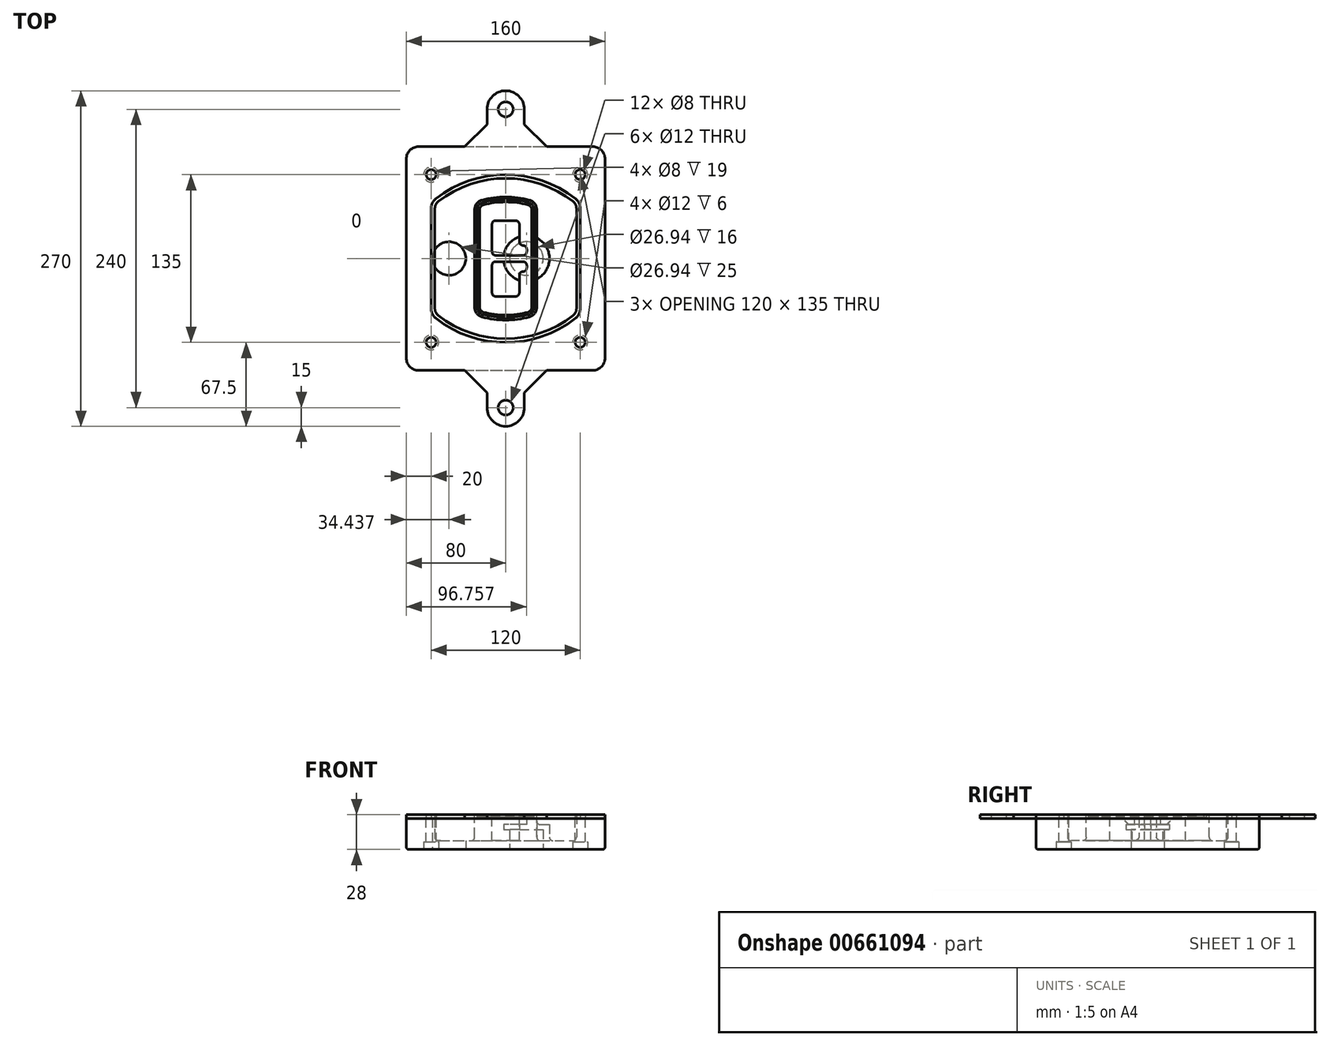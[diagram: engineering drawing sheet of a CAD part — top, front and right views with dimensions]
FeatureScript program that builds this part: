
annotation { "Feature Type Name" : "Feature", "Feature Type Description" : "" }
export const myFeature = defineFeature(function(context is Context, id is Id, definition is map)
    precondition{}
    {
        {
            var Q0;
            Q0=qCreatedBy(makeId("Top.planeOp"),FACE);
            var sketch = newSketch(context, id + "F0", { "sketchPlane" : qUnion([Q0])});
            skPoint(sketch, "E0.rect.middle", {"position": v(0, 0) * mm});
            skLineSegment(sketch, "E1.bottom", {"start": v(-70, -90) * mm, "end": v(70, -90) * mm});
            skLineSegment(sketch, "E1.top", {"start": v(-70, 90) * mm, "end": v(70, 90) * mm});
            skLineSegment(sketch, "E1.left", {"start": v(-80, -80) * mm, "end": v(-80, 80) * mm});
            skLineSegment(sketch, "E1.right", {"start": v(80, -80) * mm, "end": v(80, 80) * mm});
            skLineSegment(sketch, "E2", {"start": v(-80, 90) * mm, "end": v(80, -90) * mm, "construction": true});
            skLineSegment(sketch, "E3", {"start": v(80, 90) * mm, "end": v(-80, -90) * mm, "construction": true});
            skCircle(sketch, "E4", {"center": v(-60, 67.5) * mm, "radius": 4 * mm});
            skCircle(sketch, "E5", {"center": v(60, 67.5) * mm, "radius": 4 * mm});
            skCircle(sketch, "E6", {"center": v(60, -67.5) * mm, "radius": 4 * mm});
            skCircle(sketch, "E7", {"center": v(-60, -67.5) * mm, "radius": 4 * mm});
            skLineSegment(sketch, "E8", {"start": v(-60, 67.5) * mm, "end": v(60, 67.5) * mm, "construction": true});
            skLineSegment(sketch, "E9", {"start": v(60, 67.5) * mm, "end": v(60, -67.5) * mm, "construction": true});
            skLineSegment(sketch, "E10", {"start": v(60, -67.5) * mm, "end": v(-60, -67.5) * mm, "construction": true});
            skLineSegment(sketch, "E11", {"start": v(-60, -67.5) * mm, "end": v(-60, 67.5) * mm, "construction": true});
            skLineSegment(sketch, "E12", {"start": v(-60, 40.3) * mm, "end": v(-60, -40.3) * mm});
            skLineSegment(sketch, "E13", {"start": v(60, 40.3) * mm, "end": v(60, -40.3) * mm});
            skArc(sketch, "E14", {"start": v(56.15, 48.18) * mm, "mid": v(0, 67.5) * mm, "end": v(-56.15, 48.18) * mm});
            skArc(sketch, "E15", {"start": v(-56.15, -48.18) * mm, "mid": v(0, -67.5) * mm, "end": v(56.15, -48.18) * mm});
            skLineSegment(sketch, "E16", {"start": v(-60, 0) * mm, "end": v(60, 0) * mm, "construction": true});
            skPoint(sketch, "E17.visualSharp", {"position": v(-60, -45) * mm});
            skArc(sketch, "E17.filletArc", {"start": v(-60, -40.3) * mm, "mid": v(-58.99, -44.68) * mm, "end": v(-56.15, -48.18) * mm});
            skPoint(sketch, "E18.visualSharp", {"position": v(-60, 45) * mm});
            skArc(sketch, "E18.filletArc", {"start": v(-56.15, 48.18) * mm, "mid": v(-58.99, 44.68) * mm, "end": v(-60, 40.3) * mm});
            skPoint(sketch, "E19.visualSharp", {"position": v(60, 45) * mm});
            skArc(sketch, "E19.filletArc", {"start": v(60, 40.3) * mm, "mid": v(58.99, 44.68) * mm, "end": v(56.15, 48.18) * mm});
            skPoint(sketch, "E20.visualSharp", {"position": v(60, -45) * mm});
            skArc(sketch, "E20.filletArc", {"start": v(56.15, -48.18) * mm, "mid": v(58.99, -44.68) * mm, "end": v(60, -40.3) * mm});
            skPoint(sketch, "E21.visualSharp", {"position": v(-80, 90) * mm});
            skArc(sketch, "E21.filletArc", {"start": v(-70, 90) * mm, "mid": v(-77.07, 87.07) * mm, "end": v(-80, 80) * mm});
            skPoint(sketch, "E22.visualSharp", {"position": v(80, 90) * mm});
            skArc(sketch, "E22.filletArc", {"start": v(80, 80) * mm, "mid": v(77.07, 87.07) * mm, "end": v(70, 90) * mm});
            skPoint(sketch, "E23.visualSharp", {"position": v(80, -90) * mm});
            skArc(sketch, "E23.filletArc", {"start": v(70, -90) * mm, "mid": v(77.07, -87.07) * mm, "end": v(80, -80) * mm});
            skPoint(sketch, "E24.visualSharp", {"position": v(-80, -90) * mm});
            skArc(sketch, "E24.filletArc", {"start": v(-80, -80) * mm, "mid": v(-77.07, -87.07) * mm, "end": v(-70, -90) * mm});
            skArc(sketch, "E25.0", {"start": v(57, 40.3) * mm, "mid": v(56.3, 43.36) * mm, "end": v(54.3, 45.81) * mm});
            skLineSegment(sketch, "E25.1", {"start": v(57, 40.3) * mm, "end": v(57, -40.3) * mm});
            skArc(sketch, "E25.2", {"start": v(54.3, -45.81) * mm, "mid": v(56.3, -43.36) * mm, "end": v(57, -40.3) * mm});
            skArc(sketch, "E25.3", {"start": v(-54.3, -45.81) * mm, "mid": v(0, -64.5) * mm, "end": v(54.3, -45.81) * mm});
            skArc(sketch, "E25.4", {"start": v(-57, -40.3) * mm, "mid": v(-56.3, -43.36) * mm, "end": v(-54.3, -45.81) * mm});
            skArc(sketch, "E25.5", {"start": v(54.3, 45.81) * mm, "mid": v(0, 64.5) * mm, "end": v(-54.3, 45.81) * mm});
            skLineSegment(sketch, "E25.6", {"start": v(-57, 40.3) * mm, "end": v(-57, -40.3) * mm});
            skArc(sketch, "E25.7", {"start": v(-54.3, 45.81) * mm, "mid": v(-56.3, 43.36) * mm, "end": v(-57, 40.3) * mm});
            skArc(sketch, "E26.0", {"start": v(-58.62, 51.33) * mm, "mid": v(-62.58, 46.43) * mm, "end": v(-64, 40.3) * mm});
            skArc(sketch, "E26.1", {"start": v(58.62, 51.33) * mm, "mid": v(0, 71.5) * mm, "end": v(-58.62, 51.33) * mm});
            skArc(sketch, "E26.2", {"start": v(64, 40.3) * mm, "mid": v(62.58, 46.43) * mm, "end": v(58.62, 51.33) * mm});
            skLineSegment(sketch, "E26.3", {"start": v(64, 40.3) * mm, "end": v(64, -40.3) * mm});
            skArc(sketch, "E26.4", {"start": v(58.62, -51.33) * mm, "mid": v(62.58, -46.43) * mm, "end": v(64, -40.3) * mm});
            skLineSegment(sketch, "E26.5", {"start": v(-64, 40.3) * mm, "end": v(-64, -40.3) * mm});
            skArc(sketch, "E26.6", {"start": v(-58.62, -51.33) * mm, "mid": v(0, -71.5) * mm, "end": v(58.62, -51.33) * mm});
            skArc(sketch, "E26.7", {"start": v(-64, -40.3) * mm, "mid": v(-62.58, -46.43) * mm, "end": v(-58.62, -51.33) * mm});
            skSolve(sketch);
        }
        {
            var Q0;
            Q0=makeQuery(id+"F0.imprint","IMPRINT",FACE,{"disambiguationData":[TD([[makeQuery(id+"F0.imprint","IMPRINT",EDGE,{"derivedFrom":sQuery(id+"F0.wireOp",EDGE,"E1.bottom")}),1.0]])]});
            var Q1;
            Q1=makeQuery(id+"F0.imprint","IMPRINT",FACE,{"disambiguationData":[TD([[makeQuery(id+"F0.imprint","IMPRINT",EDGE,{"derivedFrom":sQuery(id+"F0.wireOp",EDGE,"E12")}),1.0]])]});
            var Q2;
            Q2=makeQuery(id+"F0.imprint","IMPRINT",FACE,{"disambiguationData":[TD([[makeQuery(id+"F0.imprint","IMPRINT",EDGE,{"derivedFrom":sQuery(id+"F0.wireOp",EDGE,"E25.0")}),1.0]])]});
            var Q3;
            Q3=makeQuery(id+"F0.imprint","IMPRINT",FACE,{"disambiguationData":[TD([[makeQuery(id+"F0.imprint","IMPRINT",EDGE,{"derivedFrom":sQuery(id+"F0.wireOp",EDGE,"E12")}),-1.0]])]});
            extrude(context, id + "F1", {"entities" : qUnion([Q0, Q1, Q2, Q3]), "oppositeDirection" : true, "depth" : 25 * mm});
        }
        {
            var Q0;
            Q0=makeQuery(id+"F0.imprint","IMPRINT",FACE,{"disambiguationData":[TD([[makeQuery(id+"F0.imprint","IMPRINT",EDGE,{"derivedFrom":sQuery(id+"F0.wireOp",EDGE,"E12")}),1.0]])]});
            extrude(context, id + "F2", {"entities" : qUnion([Q0]), "operationType" : NewBodyOperationType.ADD, "depth" : 3 * mm});
        }
        {
            var Q0;
            Q0=makeQuery(id+"F0.imprint","IMPRINT",FACE,{"disambiguationData":[TD([[makeQuery(id+"F0.imprint","IMPRINT",EDGE,{"derivedFrom":sQuery(id+"F0.wireOp",EDGE,"E25.0")}),1.0]])]});
            extrude(context, id + "F3", {"entities" : qUnion([Q0]), "operationType" : NewBodyOperationType.REMOVE, "oppositeDirection" : true, "depth" : 18 * mm});
        }
        {
            var Q0;
            Q0=makeQuery(id+"F2.opExtrude","CAP_FACE",FACE,{"disambiguationData":[OSD([sQuery(id+"F0.wireOp",EDGE,"E12"),sQuery(id+"F0.wireOp",EDGE,"E13"),sQuery(id+"F0.wireOp",EDGE,"E14"),sQuery(id+"F0.wireOp",EDGE,"E15"),sQuery(id+"F0.wireOp",EDGE,"E17.filletArc"),sQuery(id+"F0.wireOp",EDGE,"E18.filletArc"),sQuery(id+"F0.wireOp",EDGE,"E19.filletArc"),sQuery(id+"F0.wireOp",EDGE,"E20.filletArc"),sQuery(id+"F0.wireOp",EDGE,"E25.0"),sQuery(id+"F0.wireOp",EDGE,"E25.1"),sQuery(id+"F0.wireOp",EDGE,"E25.2"),sQuery(id+"F0.wireOp",EDGE,"E25.3"),sQuery(id+"F0.wireOp",EDGE,"E25.4"),sQuery(id+"F0.wireOp",EDGE,"E25.5"),sQuery(id+"F0.wireOp",EDGE,"E25.6"),sQuery(id+"F0.wireOp",EDGE,"E25.7")])],"isStart":false});
            var sketch = newSketch(context, id + "F4", { "sketchPlane" : qUnion([Q0])});
            skArc(sketch, "E27.0", {"start": v(-19.08, -46.97) * mm, "mid": v(0, -49.5) * mm, "end": v(19.08, -46.97) * mm});
            skArc(sketch, "E28.0", {"start": v(19.08, 46.97) * mm, "mid": v(0, 49.5) * mm, "end": v(-19.08, 46.97) * mm});
            skLineSegment(sketch, "E29", {"start": v(-25, 39.25) * mm, "end": v(-25, -39.25) * mm});
            skLineSegment(sketch, "E30", {"start": v(25, 39.25) * mm, "end": v(25, -39.25) * mm});
            skLineSegment(sketch, "E31", {"start": v(-25, 45.1) * mm, "end": v(25, 45.1) * mm, "construction": true});
            skLineSegment(sketch, "E32", {"start": v(-25, -45.1) * mm, "end": v(25, -45.1) * mm, "construction": true});
            skPoint(sketch, "E33.visualSharp", {"position": v(-25, 45.1) * mm});
            skArc(sketch, "E33.filletArc", {"start": v(-19.08, 46.97) * mm, "mid": v(-23.35, 44.11) * mm, "end": v(-25, 39.25) * mm});
            skPoint(sketch, "E34.visualSharp", {"position": v(25, 45.1) * mm});
            skArc(sketch, "E34.filletArc", {"start": v(25, 39.25) * mm, "mid": v(23.35, 44.11) * mm, "end": v(19.08, 46.97) * mm});
            skPoint(sketch, "E35.visualSharp", {"position": v(25, -45.1) * mm});
            skArc(sketch, "E35.filletArc", {"start": v(19.08, -46.97) * mm, "mid": v(23.35, -44.11) * mm, "end": v(25, -39.25) * mm});
            skPoint(sketch, "E36.visualSharp", {"position": v(-25, -45.1) * mm});
            skArc(sketch, "E36.filletArc", {"start": v(-25, -39.25) * mm, "mid": v(-23.35, -44.11) * mm, "end": v(-19.08, -46.97) * mm});
            skArc(sketch, "E37.0", {"start": v(54.3, 45.81) * mm, "mid": v(0, 64.5) * mm, "end": v(-54.3, 45.81) * mm});
            skArc(sketch, "E37.1", {"start": v(-54.3, 45.81) * mm, "mid": v(-56.3, 43.36) * mm, "end": v(-57, 40.3) * mm});
            skLineSegment(sketch, "E37.2", {"start": v(-57, 40.3) * mm, "end": v(-57, -40.3) * mm});
            skArc(sketch, "E37.3", {"start": v(-57, -40.3) * mm, "mid": v(-56.3, -43.36) * mm, "end": v(-54.3, -45.81) * mm});
            skArc(sketch, "E37.4", {"start": v(-54.3, -45.81) * mm, "mid": v(0, -64.5) * mm, "end": v(54.3, -45.81) * mm});
            skArc(sketch, "E37.5", {"start": v(54.3, -45.81) * mm, "mid": v(56.3, -43.36) * mm, "end": v(57, -40.3) * mm});
            skLineSegment(sketch, "E37.6", {"start": v(57, 40.3) * mm, "end": v(57, -40.3) * mm});
            skArc(sketch, "E37.7", {"start": v(57, 40.3) * mm, "mid": v(56.3, 43.36) * mm, "end": v(54.3, 45.81) * mm});
            skLineSegment(sketch, "E38.0", {"start": v(23, 39.25) * mm, "end": v(23, -39.25) * mm});
            skArc(sketch, "E38.1", {"start": v(18.56, -45.04) * mm, "mid": v(21.76, -42.9) * mm, "end": v(23, -39.25) * mm});
            skArc(sketch, "E38.2", {"start": v(-18.56, -45.04) * mm, "mid": v(0, -47.5) * mm, "end": v(18.56, -45.04) * mm});
            skArc(sketch, "E38.3", {"start": v(-23, -39.25) * mm, "mid": v(-21.76, -42.9) * mm, "end": v(-18.56, -45.04) * mm});
            skLineSegment(sketch, "E38.4", {"start": v(-23, 39.25) * mm, "end": v(-23, -39.25) * mm});
            skArc(sketch, "E38.5", {"start": v(23, 39.25) * mm, "mid": v(21.76, 42.9) * mm, "end": v(18.56, 45.04) * mm});
            skArc(sketch, "E38.6", {"start": v(-18.56, 45.04) * mm, "mid": v(-21.76, 42.9) * mm, "end": v(-23, 39.25) * mm});
            skArc(sketch, "E38.7", {"start": v(18.56, 45.04) * mm, "mid": v(0, 47.5) * mm, "end": v(-18.56, 45.04) * mm});
            skArc(sketch, "E39.0", {"start": v(21, 39.25) * mm, "mid": v(20.18, 41.68) * mm, "end": v(18.04, 43.1) * mm});
            skLineSegment(sketch, "E39.1", {"start": v(21, 39.25) * mm, "end": v(21, -39.25) * mm});
            skArc(sketch, "E39.2", {"start": v(18.04, -43.1) * mm, "mid": v(20.18, -41.68) * mm, "end": v(21, -39.25) * mm});
            skArc(sketch, "E39.3", {"start": v(-18.04, -43.1) * mm, "mid": v(0, -45.5) * mm, "end": v(18.04, -43.1) * mm});
            skArc(sketch, "E39.4", {"start": v(-21, -39.25) * mm, "mid": v(-20.18, -41.68) * mm, "end": v(-18.04, -43.1) * mm});
            skArc(sketch, "E39.5", {"start": v(18.04, 43.1) * mm, "mid": v(0, 45.5) * mm, "end": v(-18.04, 43.1) * mm});
            skLineSegment(sketch, "E39.6", {"start": v(-21, 39.25) * mm, "end": v(-21, -39.25) * mm});
            skArc(sketch, "E39.7", {"start": v(-18.04, 43.1) * mm, "mid": v(-20.18, 41.68) * mm, "end": v(-21, 39.25) * mm});
            skLineSegment(sketch, "E40", {"start": v(-25, 0) * mm, "end": v(25, 0) * mm, "construction": true});
            skLineSegment(sketch, "E41", {"start": v(-11, 5.5) * mm, "end": v(-11, 27.5) * mm});
            skLineSegment(sketch, "E42", {"start": v(-8, 30.5) * mm, "end": v(8, 30.5) * mm});
            skLineSegment(sketch, "E43", {"start": v(11, 27.5) * mm, "end": v(11, 13.5) * mm});
            skLineSegment(sketch, "E44", {"start": v(14, 10.5) * mm, "end": v(14, 10.5) * mm});
            skLineSegment(sketch, "E45", {"start": v(17, 7.5) * mm, "end": v(17, 5.5) * mm});
            skLineSegment(sketch, "E46", {"start": v(14, 2.5) * mm, "end": v(-8, 2.5) * mm});
            skPoint(sketch, "E47.visualSharp", {"position": v(-11, 30.5) * mm});
            skArc(sketch, "E47.filletArc", {"start": v(-8, 30.5) * mm, "mid": v(-10.12, 29.62) * mm, "end": v(-11, 27.5) * mm});
            skPoint(sketch, "E48.visualSharp", {"position": v(11, 30.5) * mm});
            skArc(sketch, "E48.filletArc", {"start": v(11, 27.5) * mm, "mid": v(10.12, 29.62) * mm, "end": v(8, 30.5) * mm});
            skPoint(sketch, "E49.visualSharp", {"position": v(11, 10.5) * mm});
            skArc(sketch, "E49.filletArc", {"start": v(11, 13.5) * mm, "mid": v(11.88, 11.38) * mm, "end": v(14, 10.5) * mm});
            skPoint(sketch, "E50.visualSharp", {"position": v(17, 10.5) * mm});
            skArc(sketch, "E50.filletArc", {"start": v(17, 7.5) * mm, "mid": v(16.12, 9.62) * mm, "end": v(14, 10.5) * mm});
            skPoint(sketch, "E51.visualSharp", {"position": v(17, 2.5) * mm});
            skArc(sketch, "E51.filletArc", {"start": v(14, 2.5) * mm, "mid": v(16.12, 3.38) * mm, "end": v(17, 5.5) * mm});
            skPoint(sketch, "E52.visualSharp", {"position": v(-11, 2.5) * mm});
            skArc(sketch, "E52.filletArc", {"start": v(-11, 5.5) * mm, "mid": v(-10.12, 3.38) * mm, "end": v(-8, 2.5) * mm});
            skLineSegment(sketch, "E53.0.MirrorCS", {"start": v(14, -2.5) * mm, "end": v(-8, -2.5) * mm});
            skArc(sketch, "E54.0.MirrorCS", {"start": v(-11, -5.5) * mm, "mid": v(-10.12, -3.38) * mm, "end": v(-8, -2.5) * mm});
            skLineSegment(sketch, "E55.0.MirrorCS", {"start": v(-11, -5.5) * mm, "end": v(-11, -27.5) * mm});
            skArc(sketch, "E56.0.MirrorCS", {"start": v(-8, -30.5) * mm, "mid": v(-10.12, -29.62) * mm, "end": v(-11, -27.5) * mm});
            skLineSegment(sketch, "E57.0.MirrorCS", {"start": v(-8, -30.5) * mm, "end": v(8, -30.5) * mm});
            skArc(sketch, "E58.0.MirrorCS", {"start": v(11, -27.5) * mm, "mid": v(10.12, -29.62) * mm, "end": v(8, -30.5) * mm});
            skLineSegment(sketch, "E59.0.MirrorCS", {"start": v(11, -27.5) * mm, "end": v(11, -13.5) * mm});
            skArc(sketch, "E60.0.MirrorCS", {"start": v(11, -13.5) * mm, "mid": v(11.88, -11.38) * mm, "end": v(14, -10.5) * mm});
            skArc(sketch, "E61.0.MirrorCS", {"start": v(17, -7.5) * mm, "mid": v(16.12, -9.62) * mm, "end": v(14, -10.5) * mm});
            skLineSegment(sketch, "E62.0.MirrorCS", {"start": v(17, -7.5) * mm, "end": v(17, -5.5) * mm});
            skArc(sketch, "E63.0.MirrorCS", {"start": v(14, -2.5) * mm, "mid": v(16.12, -3.38) * mm, "end": v(17, -5.5) * mm});
            skSolve(sketch);
        }
        {
            var Q0;
            Q0=makeQuery(id+"F4.imprint","IMPRINT",FACE,{"disambiguationData":[TD([[makeQuery(id+"F4.imprint","IMPRINT",EDGE,{"derivedFrom":sQuery(id+"F4.wireOp",EDGE,"E27.0")}),1.0]])]});
            var Q1;
            Q1=makeQuery(id+"F4.imprint","IMPRINT",FACE,{"disambiguationData":[TD([[makeQuery(id+"F4.imprint","IMPRINT",EDGE,{"derivedFrom":sQuery(id+"F4.wireOp",EDGE,"E38.0")}),-1.0]])]});
            var Q2;
            Q2=makeQuery(id+"F4.imprint","IMPRINT",FACE,{"disambiguationData":[TD([[makeQuery(id+"F4.imprint","IMPRINT",EDGE,{"derivedFrom":sQuery(id+"F4.wireOp",EDGE,"E39.0")}),1.0]])]});
            extrude(context, id + "F5", {"entities" : qUnion([Q0, Q1, Q2]), "operationType" : NewBodyOperationType.ADD, "endBound" : BoundingType.UP_TO_NEXT, "oppositeDirection" : true, "depth" : 25 * mm});
        }
        {
            var Q0;
            Q0=makeQuery(id+"F4.imprint","IMPRINT",FACE,{"disambiguationData":[TD([[makeQuery(id+"F4.imprint","IMPRINT",EDGE,{"derivedFrom":sQuery(id+"F4.wireOp",EDGE,"E38.0")}),-1.0]])]});
            extrude(context, id + "F6", {"entities" : qUnion([Q0]), "operationType" : NewBodyOperationType.REMOVE, "oppositeDirection" : true, "depth" : 2 * mm});
        }
        {
            var Q0;
            Q0=makeQuery(id+"F1.opExtrude","CAP_FACE",FACE,{"disambiguationData":[OSD([sQuery(id+"F0.wireOp",EDGE,"E1.bottom"),sQuery(id+"F0.wireOp",EDGE,"E1.top"),sQuery(id+"F0.wireOp",EDGE,"E1.left"),sQuery(id+"F0.wireOp",EDGE,"E1.right"),sQuery(id+"F0.wireOp",EDGE,"E4"),sQuery(id+"F0.wireOp",EDGE,"E5"),sQuery(id+"F0.wireOp",EDGE,"E6"),sQuery(id+"F0.wireOp",EDGE,"E7"),sQuery(id+"F0.wireOp",EDGE,"E21.filletArc"),sQuery(id+"F0.wireOp",EDGE,"E22.filletArc"),sQuery(id+"F0.wireOp",EDGE,"E23.filletArc"),sQuery(id+"F0.wireOp",EDGE,"E24.filletArc")])],"isStart":false});
            var sketch = newSketch(context, id + "F7", { "sketchPlane" : qUnion([Q0])});
            skCircle(sketch, "E64", {"center": v(16.76, 0) * mm, "radius": 13.47 * mm});
            skCircle(sketch, "E65", {"center": v(-45.56, 0) * mm, "radius": 13.47 * mm});
            skLineSegment(sketch, "E66", {"start": v(80, 0) * mm, "end": v(-80, 0) * mm});
            skCircle(sketch, "E67", {"center": v(16.76, 0) * mm, "radius": 18.47 * mm});
            skCircle(sketch, "E68", {"center": v(60, -67.5) * mm, "radius": 6 * mm});
            skCircle(sketch, "E69", {"center": v(-60, -67.5) * mm, "radius": 6 * mm});
            skCircle(sketch, "E70", {"center": v(-60, 67.5) * mm, "radius": 6 * mm});
            skCircle(sketch, "E71", {"center": v(60, 67.5) * mm, "radius": 6 * mm});
            skSolve(sketch);
        }
        {
            var Q0;
            {var subQ1=sQuery(id+"F7.wireOp",EDGE,"E66");var subQ4=sQuery(id+"F7.wireOp",EDGE,"E64");var subQ6=makeQuery(id+"F7.imprint","INTERSECT",VERTEX,{"disambiguationData":[OD(0.0)],"derivedFrom":[subQ4,subQ1]});Q0=makeQuery(id+"F7.imprint","IMPRINT",FACE,{"disambiguationData":[TD([[makeQuery(id+"F7.imprint","IMPRINT",EDGE,{"disambiguationData":[TD([[subQ6,-1.0]])],"derivedFrom":subQ4}),-1.0]])]});}
            var Q1;
            {var subQ0=sQuery(id+"F7.wireOp",EDGE,"E66");var subQ1=sQuery(id+"F7.wireOp",EDGE,"E64");var subQ3=makeQuery(id+"F7.imprint","INTERSECT",VERTEX,{"disambiguationData":[OD(0.0)],"derivedFrom":[subQ1,subQ0]});Q1=makeQuery(id+"F7.imprint","IMPRINT",FACE,{"disambiguationData":[TD([[makeQuery(id+"F7.imprint","IMPRINT",EDGE,{"disambiguationData":[TD([[subQ3,-1.0]])],"derivedFrom":subQ1}),1.0]])]});}
            var Q2;
            {var subQ0=sQuery(id+"F7.wireOp",EDGE,"E66");var subQ1=sQuery(id+"F7.wireOp",EDGE,"E64");var subQ3=makeQuery(id+"F7.imprint","INTERSECT",VERTEX,{"disambiguationData":[OD(0.0)],"derivedFrom":[subQ1,subQ0]});Q2=makeQuery(id+"F7.imprint","IMPRINT",FACE,{"disambiguationData":[TD([[makeQuery(id+"F7.imprint","IMPRINT",EDGE,{"disambiguationData":[TD([[subQ3,1.0]])],"derivedFrom":subQ1}),1.0]])]});}
            var Q3;
            {var subQ1=sQuery(id+"F7.wireOp",EDGE,"E66");var subQ4=sQuery(id+"F7.wireOp",EDGE,"E64");var subQ6=makeQuery(id+"F7.imprint","INTERSECT",VERTEX,{"disambiguationData":[OD(0.0)],"derivedFrom":[subQ4,subQ1]});Q3=makeQuery(id+"F7.imprint","IMPRINT",FACE,{"disambiguationData":[TD([[makeQuery(id+"F7.imprint","IMPRINT",EDGE,{"disambiguationData":[TD([[subQ6,1.0]])],"derivedFrom":subQ4}),-1.0]])]});}
            extrude(context, id + "F8", {"entities" : qUnion([Q0, Q1, Q2, Q3]), "operationType" : NewBodyOperationType.ADD, "oppositeDirection" : true, "depth" : 20 * mm});
        }
        {
            var Q0;
            {var subQ0=sQuery(id+"F7.wireOp",EDGE,"E66");var subQ1=sQuery(id+"F7.wireOp",EDGE,"E64");var subQ3=makeQuery(id+"F7.imprint","INTERSECT",VERTEX,{"disambiguationData":[OD(0.0)],"derivedFrom":[subQ1,subQ0]});Q0=makeQuery(id+"F7.imprint","IMPRINT",FACE,{"disambiguationData":[TD([[makeQuery(id+"F7.imprint","IMPRINT",EDGE,{"disambiguationData":[TD([[subQ3,-1.0]])],"derivedFrom":subQ1}),1.0]])]});}
            var Q1;
            {var subQ0=sQuery(id+"F7.wireOp",EDGE,"E66");var subQ1=sQuery(id+"F7.wireOp",EDGE,"E64");var subQ3=makeQuery(id+"F7.imprint","INTERSECT",VERTEX,{"disambiguationData":[OD(0.0)],"derivedFrom":[subQ1,subQ0]});Q1=makeQuery(id+"F7.imprint","IMPRINT",FACE,{"disambiguationData":[TD([[makeQuery(id+"F7.imprint","IMPRINT",EDGE,{"disambiguationData":[TD([[subQ3,1.0]])],"derivedFrom":subQ1}),1.0]])]});}
            extrude(context, id + "F9", {"entities" : qUnion([Q0, Q1]), "operationType" : NewBodyOperationType.REMOVE, "oppositeDirection" : true, "depth" : 16 * mm});
        }
        {
            var Q0;
            {var subQ0=sQuery(id+"F7.wireOp",EDGE,"E66");var subQ1=sQuery(id+"F7.wireOp",EDGE,"E65");var subQ3=makeQuery(id+"F7.imprint","INTERSECT",VERTEX,{"disambiguationData":[OD(0.0)],"derivedFrom":[subQ1,subQ0]});Q0=makeQuery(id+"F7.imprint","IMPRINT",FACE,{"disambiguationData":[TD([[makeQuery(id+"F7.imprint","IMPRINT",EDGE,{"disambiguationData":[TD([[subQ3,-1.0]])],"derivedFrom":subQ1}),1.0]])]});}
            var Q1;
            {var subQ0=sQuery(id+"F7.wireOp",EDGE,"E66");var subQ1=sQuery(id+"F7.wireOp",EDGE,"E65");var subQ3=makeQuery(id+"F7.imprint","INTERSECT",VERTEX,{"disambiguationData":[OD(0.0)],"derivedFrom":[subQ1,subQ0]});Q1=makeQuery(id+"F7.imprint","IMPRINT",FACE,{"disambiguationData":[TD([[makeQuery(id+"F7.imprint","IMPRINT",EDGE,{"disambiguationData":[TD([[subQ3,1.0]])],"derivedFrom":subQ1}),1.0]])]});}
            extrude(context, id + "F10", {"entities" : qUnion([Q0, Q1]), "operationType" : NewBodyOperationType.REMOVE, "oppositeDirection" : true, "depth" : 25 * mm});
        }
        {
            var Q0;
            Q0=makeQuery(id+"F7.imprint","IMPRINT",FACE,{"disambiguationData":[TD([[makeQuery(id+"F7.imprint","IMPRINT",EDGE,{"derivedFrom":sQuery(id+"F7.wireOp",EDGE,"E68")}),1.0]])]});
            var Q1;
            Q1=makeQuery(id+"F7.imprint","IMPRINT",FACE,{"disambiguationData":[TD([[makeQuery(id+"F7.imprint","IMPRINT",EDGE,{"derivedFrom":makeQuery(id+"F1.opExtrude","CAP_EDGE",EDGE,{"disambiguationData":[OSD([sQuery(id+"F0.wireOp",EDGE,"E5")])],"isStart":false})}),-1.0]])]});
            var Q2;
            Q2=makeQuery(id+"F7.imprint","IMPRINT",FACE,{"disambiguationData":[TD([[makeQuery(id+"F7.imprint","IMPRINT",EDGE,{"derivedFrom":sQuery(id+"F7.wireOp",EDGE,"E69")}),1.0]])]});
            var Q3;
            Q3=makeQuery(id+"F7.imprint","IMPRINT",FACE,{"disambiguationData":[TD([[makeQuery(id+"F7.imprint","IMPRINT",EDGE,{"derivedFrom":makeQuery(id+"F1.opExtrude","CAP_EDGE",EDGE,{"disambiguationData":[OSD([sQuery(id+"F0.wireOp",EDGE,"E4")])],"isStart":false})}),-1.0]])]});
            var Q4;
            Q4=makeQuery(id+"F7.imprint","IMPRINT",FACE,{"disambiguationData":[TD([[makeQuery(id+"F7.imprint","IMPRINT",EDGE,{"derivedFrom":sQuery(id+"F7.wireOp",EDGE,"E70")}),1.0]])]});
            var Q5;
            Q5=makeQuery(id+"F7.imprint","IMPRINT",FACE,{"disambiguationData":[TD([[makeQuery(id+"F7.imprint","IMPRINT",EDGE,{"derivedFrom":makeQuery(id+"F1.opExtrude","CAP_EDGE",EDGE,{"disambiguationData":[OSD([sQuery(id+"F0.wireOp",EDGE,"E7")])],"isStart":false})}),-1.0]])]});
            var Q6;
            Q6=makeQuery(id+"F7.imprint","IMPRINT",FACE,{"disambiguationData":[TD([[makeQuery(id+"F7.imprint","IMPRINT",EDGE,{"derivedFrom":sQuery(id+"F7.wireOp",EDGE,"E71")}),1.0]])]});
            var Q7;
            Q7=makeQuery(id+"F7.imprint","IMPRINT",FACE,{"disambiguationData":[TD([[makeQuery(id+"F7.imprint","IMPRINT",EDGE,{"derivedFrom":makeQuery(id+"F1.opExtrude","CAP_EDGE",EDGE,{"disambiguationData":[OSD([sQuery(id+"F0.wireOp",EDGE,"E6")])],"isStart":false})}),-1.0]])]});
            extrude(context, id + "F11", {"entities" : qUnion([Q0, Q1, Q2, Q3, Q4, Q5, Q6, Q7]), "operationType" : NewBodyOperationType.REMOVE, "oppositeDirection" : true, "depth" : 6 * mm});
        }
        {
            var Q0;
            Q0=makeQuery(id+"F9.boolean.opBoolean","COPY",FACE,{"derivedFrom":makeQuery(id+"F9.opExtrude","CAP_FACE",FACE,{"disambiguationData":[OSD([sQuery(id+"F7.wireOp",EDGE,"E64")])],"isStart":false})});
            var sketch = newSketch(context, id + "F12", { "sketchPlane" : qUnion([Q0])});
            skArc(sketch, "E72.0", {"start": v(11, 17.55) * mm, "mid": v(2.57, 11.82) * mm, "end": v(-1.54, 2.5) * mm});
            skArc(sketch, "E72.1", {"start": v(-1.54, -2.5) * mm, "mid": v(2.57, -11.82) * mm, "end": v(11, -17.55) * mm});
            skLineSegment(sketch, "E73", {"start": v(-1.54, -2.5) * mm, "end": v(14, -2.5) * mm});
            skLineSegment(sketch, "E74.0", {"start": v(14, 2.5) * mm, "end": v(-1.54, 2.5) * mm});
            skArc(sketch, "E74.1", {"start": v(14, 2.5) * mm, "mid": v(16.12, 3.38) * mm, "end": v(17, 5.5) * mm});
            skLineSegment(sketch, "E74.2", {"start": v(17, 7.5) * mm, "end": v(17, 5.5) * mm});
            skArc(sketch, "E74.3", {"start": v(17, 7.5) * mm, "mid": v(16.12, 9.62) * mm, "end": v(14, 10.5) * mm});
            skArc(sketch, "E74.4", {"start": v(11, 13.5) * mm, "mid": v(11.88, 11.38) * mm, "end": v(14, 10.5) * mm});
            skLineSegment(sketch, "E74.5", {"start": v(11, 17.55) * mm, "end": v(11, 13.5) * mm});
            skLineSegment(sketch, "E74.7", {"start": v(14, -2.5) * mm, "end": v(-1.54, -2.5) * mm});
            skArc(sketch, "E74.8", {"start": v(14, -2.5) * mm, "mid": v(16.12, -3.38) * mm, "end": v(17, -5.5) * mm});
            skLineSegment(sketch, "E74.9", {"start": v(17, -7.5) * mm, "end": v(17, -5.5) * mm});
            skArc(sketch, "E74.10", {"start": v(17, -7.5) * mm, "mid": v(16.12, -9.62) * mm, "end": v(14, -10.5) * mm});
            skArc(sketch, "E74.11", {"start": v(11, -13.5) * mm, "mid": v(11.88, -11.38) * mm, "end": v(14, -10.5) * mm});
            skLineSegment(sketch, "E74.12", {"start": v(11, -17.55) * mm, "end": v(11, -13.5) * mm});
            skPoint(sketch, "E75.orphan", {"position": v(11, -27.5) * mm});
            skPoint(sketch, "E76.orphan", {"position": v(-8, -2.5) * mm});
            skPoint(sketch, "E77.orphan", {"position": v(-8, 2.5) * mm});
            skPoint(sketch, "E78.orphan", {"position": v(11, 27.5) * mm});
            skSolve(sketch);
        }
        {
            var Q0;
            {var subQ7=sQuery(id+"F12.wireOp",EDGE,"E72.0");var subQ14=sQuery(id+"F12.wireOp",EDGE,"E72.1");var subQ16=sQuery(id+"F12.wireOp",EDGE,"E74.1");var subQ18=sQuery(id+"F12.wireOp",EDGE,"E74.8");Q0=qUnion([makeQuery(id+"F12.imprint","IMPRINT",FACE,{"disambiguationData":[TD([[makeQuery(id+"F12.imprint","IMPRINT",EDGE,{"derivedFrom":subQ7}),1.0]])]}),makeQuery(id+"F12.imprint","IMPRINT",FACE,{"disambiguationData":[TD([[makeQuery(id+"F12.imprint","IMPRINT",EDGE,{"derivedFrom":subQ14}),1.0]])]}),makeQuery(id+"F12.imprint","IMPRINT",FACE,{"disambiguationData":[TD([[makeQuery(id+"F12.imprint","IMPRINT",EDGE,{"derivedFrom":subQ16}),1.0]])]}),makeQuery(id+"F12.imprint","IMPRINT",FACE,{"disambiguationData":[TD([[makeQuery(id+"F12.imprint","IMPRINT",EDGE,{"derivedFrom":subQ18}),-1.0]])]})]);}
            var Q1;
            Q1=makeQuery(id+"F5.boolean.opBoolean","SPLIT",FACE,{"disambiguationData":[TD([makeQuery(id+"F5.opExtrude","SWEPT_FACE",FACE,{"disambiguationData":[OSD([sQuery(id+"F4.wireOp",EDGE,"E41")])]})])],"derivedFrom":makeQuery(id+"F3.boolean.opBoolean","COPY",FACE,{"derivedFrom":makeQuery(id+"F3.opExtrude","CAP_FACE",FACE,{"disambiguationData":[OSD([sQuery(id+"F0.wireOp",EDGE,"E25.0"),sQuery(id+"F0.wireOp",EDGE,"E25.1"),sQuery(id+"F0.wireOp",EDGE,"E25.2"),sQuery(id+"F0.wireOp",EDGE,"E25.3"),sQuery(id+"F0.wireOp",EDGE,"E25.4"),sQuery(id+"F0.wireOp",EDGE,"E25.5"),sQuery(id+"F0.wireOp",EDGE,"E25.6"),sQuery(id+"F0.wireOp",EDGE,"E25.7")])],"isStart":false})})});
            extrude(context, id + "F13", {"entities" : qUnion([Q0]), "operationType" : NewBodyOperationType.REMOVE, "endBound" : BoundingType.UP_TO_SURFACE, "endBoundEntityFace" : qUnion([Q1]), "depth" : 25 * mm});
        }
        {
            var Q0;
            Q0=makeQuery(id+"F3.boolean.opBoolean","COPY",EDGE,{"derivedFrom":makeQuery(id+"F3.opExtrude","CAP_EDGE",EDGE,{"disambiguationData":[OSD([sQuery(id+"F0.wireOp",EDGE,"E25.6")])],"isStart":false})});
            var Q1;
            Q1=makeQuery(id+"F8.boolean.opBoolean","INTERSECT",EDGE,{"derivedFrom":[makeQuery(id+"F5.opExtrude","SWEPT_FACE",FACE,{"disambiguationData":[OSD([sQuery(id+"F4.wireOp",EDGE,"E30")])]}),makeQuery(id+"F8.opExtrude","CAP_FACE",FACE,{"disambiguationData":[OSD([sQuery(id+"F7.wireOp",EDGE,"E67")])],"isStart":false})]});
            var Q2;
            Q2=makeQuery(id+"F8.boolean.opBoolean","INTERSECT",EDGE,{"disambiguationData":[OD(1.0)],"derivedFrom":[makeQuery(id+"F5.opExtrude","SWEPT_FACE",FACE,{"disambiguationData":[OSD([sQuery(id+"F4.wireOp",EDGE,"E30")])]}),makeQuery(id+"F8.opExtrude","SWEPT_FACE",FACE,{"disambiguationData":[OSD([sQuery(id+"F7.wireOp",EDGE,"E67")])]})]});
            var Q3;
            {var subQ0=sQuery(id+"F4.wireOp",EDGE,"E30");Q3=makeQuery(id+"F8.boolean.opBoolean","SPLIT",EDGE,{"disambiguationData":[TD([makeQuery(id+"F5.opExtrude","SWEPT_FACE",FACE,{"disambiguationData":[OSD([sQuery(id+"F4.wireOp",EDGE,"E35.filletArc")])]})])],"derivedFrom":makeQuery(id+"F5.opExtrude","CAP_EDGE",EDGE,{"disambiguationData":[OSD([subQ0])],"isStart":false})});}
            var Q4;
            {var subQ0=sQuery(id+"F0.wireOp",EDGE,"E25.7");var subQ1=sQuery(id+"F0.wireOp",EDGE,"E25.1");var subQ2=sQuery(id+"F0.wireOp",EDGE,"E25.6");var subQ3=sQuery(id+"F0.wireOp",EDGE,"E25.5");var subQ4=sQuery(id+"F0.wireOp",EDGE,"E25.4");var subQ5=sQuery(id+"F0.wireOp",EDGE,"E25.0");var subQ6=sQuery(id+"F0.wireOp",EDGE,"E25.2");var subQ7=sQuery(id+"F0.wireOp",EDGE,"E25.3");Q4=makeQuery(id+"F8.boolean.opBoolean","INTERSECT",EDGE,{"derivedFrom":[makeQuery(id+"F5.boolean.opBoolean","SPLIT",FACE,{"disambiguationData":[TD([makeQuery(id+"F2.opExtrude","SWEPT_FACE",FACE,{"disambiguationData":[OSD([subQ5])]})])],"derivedFrom":makeQuery(id+"F3.boolean.opBoolean","COPY",FACE,{"derivedFrom":makeQuery(id+"F3.opExtrude","CAP_FACE",FACE,{"disambiguationData":[OSD([subQ5,subQ1,subQ6,subQ7,subQ4,subQ3,subQ2,subQ0])],"isStart":false})})}),makeQuery(id+"F8.opExtrude","SWEPT_FACE",FACE,{"disambiguationData":[OSD([sQuery(id+"F7.wireOp",EDGE,"E67")])]})]});}
            var Q5;
            Q5=makeQuery(id+"F8.boolean.opBoolean","INTERSECT",EDGE,{"disambiguationData":[OD(0.0)],"derivedFrom":[makeQuery(id+"F5.opExtrude","SWEPT_FACE",FACE,{"disambiguationData":[OSD([sQuery(id+"F4.wireOp",EDGE,"E30")])]}),makeQuery(id+"F8.opExtrude","SWEPT_FACE",FACE,{"disambiguationData":[OSD([sQuery(id+"F7.wireOp",EDGE,"E67")])]})]});
            fillet(context, id + "F14", {"entities" : qUnion([Q0, Q1, Q2, Q3, Q4, Q5]), "radius" : 3 * mm, "tangentPropagation" : true, "allowEdgeOverflow" : false});
        }
        {
            var Q0;
            Q0=makeQuery(id+"F1.opExtrude","CAP_EDGE",EDGE,{"disambiguationData":[OSD([sQuery(id+"F0.wireOp",EDGE,"E1.bottom")])],"isStart":false});
            fillet(context, id + "F15", {"entities" : qUnion([Q0]), "radius" : 2 * mm, "tangentPropagation" : true, "allowEdgeOverflow" : false});
        }
        {
            var Q0;
            {var subQ0=sQuery(id+"F0.wireOp",EDGE,"E21.filletArc");var subQ1=sQuery(id+"F0.wireOp",EDGE,"E7");var subQ2=sQuery(id+"F0.wireOp",EDGE,"E6");var subQ3=sQuery(id+"F0.wireOp",EDGE,"E5");var subQ4=sQuery(id+"F0.wireOp",EDGE,"E4");var subQ5=sQuery(id+"F0.wireOp",EDGE,"E22.filletArc");var subQ6=sQuery(id+"F0.wireOp",EDGE,"E1.bottom");var subQ7=sQuery(id+"F0.wireOp",EDGE,"E1.right");var subQ8=sQuery(id+"F0.wireOp",EDGE,"E1.top");var subQ9=sQuery(id+"F0.wireOp",EDGE,"E1.left");var subQ10=sQuery(id+"F0.wireOp",EDGE,"E23.filletArc");var subQ11=sQuery(id+"F0.wireOp",EDGE,"E24.filletArc");Q0=makeQuery(id+"F2.boolean.opBoolean","SPLIT",FACE,{"disambiguationData":[TD([makeQuery(id+"F1.opExtrude","SWEPT_FACE",FACE,{"disambiguationData":[OSD([subQ6])]})])],"derivedFrom":makeQuery(id+"F1.opExtrude","CAP_FACE",FACE,{"disambiguationData":[OSD([subQ6,subQ8,subQ9,subQ7,subQ4,subQ3,subQ2,subQ1,subQ0,subQ5,subQ10,subQ11])],"isStart":true})});}
            var sketch = newSketch(context, id + "F16", { "sketchPlane" : qUnion([Q0])});
            skLineSegment(sketch, "E79", {"start": v(0, 90) * mm, "end": v(0, 120) * mm, "construction": true});
            skCircle(sketch, "E80", {"center": v(0, 120) * mm, "radius": 6 * mm});
            skArc(sketch, "E81", {"start": v(15, 120) * mm, "mid": v(0, 135) * mm, "end": v(-15, 120) * mm});
            skLineSegment(sketch, "E82", {"start": v(-15, 120) * mm, "end": v(-15, 108) * mm});
            skLineSegment(sketch, "E83", {"start": v(15, 120) * mm, "end": v(15, 108) * mm});
            skLineSegment(sketch, "E84", {"start": v(-15, 108) * mm, "end": v(-33, 90) * mm});
            skLineSegment(sketch, "E85", {"start": v(15, 108) * mm, "end": v(33, 90) * mm});
            skLineSegment(sketch, "E86", {"start": v(-80, 0) * mm, "end": v(80, 0) * mm, "construction": true});
            skArc(sketch, "E87.MirrorCS", {"start": v(-15, 120) * mm, "mid": v(0, 135) * mm, "end": v(15, 120) * mm});
            skLineSegment(sketch, "E88.MirrorCS", {"start": v(15, -120) * mm, "end": v(15, -108) * mm});
            skCircle(sketch, "E89.MirrorC", {"center": v(0, -120) * mm, "radius": 6 * mm});
            skLineSegment(sketch, "E90.MirrorCS", {"start": v(15, -108) * mm, "end": v(33, -90) * mm});
            skLineSegment(sketch, "E91.MirrorCS", {"start": v(-15, -120) * mm, "end": v(-15, -108) * mm});
            skArc(sketch, "E92.MirrorCS", {"start": v(-15, -120) * mm, "mid": v(0, -135) * mm, "end": v(15, -120) * mm});
            skLineSegment(sketch, "E93.MirrorCS", {"start": v(-15, -108) * mm, "end": v(-33, -90) * mm});
            skArc(sketch, "E94.MirrorCS", {"start": v(15, -120) * mm, "mid": v(0, -135) * mm, "end": v(-15, -120) * mm});
            skLineSegment(sketch, "E95.MirrorCS", {"start": v(0, -90) * mm, "end": v(0, -120) * mm, "construction": true});
            skLineSegment(sketch, "E96", {"start": v(33, -90) * mm, "end": v(70, -90) * mm});
            skLineSegment(sketch, "E97", {"start": v(80, -80) * mm, "end": v(80, 0) * mm});
            skArc(sketch, "E98", {"start": v(70, -90) * mm, "mid": v(77.07, -87.07) * mm, "end": v(80, -80) * mm});
            skArc(sketch, "E99", {"start": v(-80, -80) * mm, "mid": v(-77.07, -87.07) * mm, "end": v(-70, -90) * mm});
            skLineSegment(sketch, "E100", {"start": v(-33, -90) * mm, "end": v(-70, -90) * mm});
            skLineSegment(sketch, "E101", {"start": v(-80, -80) * mm, "end": v(-80, 80) * mm});
            skLineSegment(sketch, "E102", {"start": v(80, 0) * mm, "end": v(80, 80) * mm});
            skLineSegment(sketch, "E103", {"start": v(70, 90) * mm, "end": v(33, 90) * mm});
            skLineSegment(sketch, "E104", {"start": v(-33, 90) * mm, "end": v(-70, 90) * mm});
            skArc(sketch, "E105", {"start": v(80, 80) * mm, "mid": v(77.07, 87.07) * mm, "end": v(70, 90) * mm});
            skArc(sketch, "E106", {"start": v(-70, 90) * mm, "mid": v(-77.07, 87.07) * mm, "end": v(-80, 80) * mm});
            skLineSegment(sketch, "E107", {"start": v(-60, 40.3) * mm, "end": v(-60, -40.3) * mm});
            skLineSegment(sketch, "E108", {"start": v(60, 40.3) * mm, "end": v(60, -40.3) * mm});
            skArc(sketch, "E109", {"start": v(60, 40.3) * mm, "mid": v(58.99, 44.68) * mm, "end": v(56.15, 48.18) * mm});
            skArc(sketch, "E110", {"start": v(-56.15, 48.18) * mm, "mid": v(-58.99, 44.68) * mm, "end": v(-60, 40.3) * mm});
            skArc(sketch, "E111", {"start": v(-56.15, 48.18) * mm, "mid": v(0, 67.5) * mm, "end": v(56.15, 48.18) * mm});
            skArc(sketch, "E112", {"start": v(-60, -40.3) * mm, "mid": v(-58.99, -44.68) * mm, "end": v(-56.15, -48.18) * mm});
            skArc(sketch, "E113", {"start": v(56.15, -48.18) * mm, "mid": v(58.99, -44.68) * mm, "end": v(60, -40.3) * mm});
            skArc(sketch, "E114", {"start": v(-56.15, -48.18) * mm, "mid": v(0, -67.5) * mm, "end": v(56.15, -48.18) * mm});
            skCircle(sketch, "E115", {"center": v(-60, -67.5) * mm, "radius": 4 * mm});
            skCircle(sketch, "E116", {"center": v(-60, 67.5) * mm, "radius": 4 * mm});
            skCircle(sketch, "E117", {"center": v(60, 67.5) * mm, "radius": 4 * mm});
            skCircle(sketch, "E118", {"center": v(60, -67.5) * mm, "radius": 4 * mm});
            skSolve(sketch);
        }
        {
            var Q0;
            Q0=makeQuery(id+"F16.imprint","IMPRINT",FACE,{"disambiguationData":[TD([[makeQuery(id+"F16.imprint","IMPRINT",EDGE,{"derivedFrom":sQuery(id+"F16.wireOp",EDGE,"E88.MirrorCS")}),1.0]])]});
            var Q1;
            {var subQ5=sQuery(id+"F16.wireOp",EDGE,"E96");Q1=makeQuery(id+"F16.imprint","IMPRINT",FACE,{"disambiguationData":[TD([[makeQuery(id+"F16.imprint","IMPRINT",EDGE,{"derivedFrom":subQ5}),1.0]])]});}
            var Q2;
            {var subQ1=sQuery(id+"F16.wireOp",EDGE,"E84");Q2=makeQuery(id+"F16.imprint","IMPRINT",FACE,{"disambiguationData":[TD([[makeQuery(id+"F16.imprint","IMPRINT",EDGE,{"derivedFrom":subQ1}),1.0]])]});}
            var Q3;
            Q3=makeQuery(id+"F2.opExtrude","CAP_FACE",FACE,{"disambiguationData":[OSD([sQuery(id+"F0.wireOp",EDGE,"E12"),sQuery(id+"F0.wireOp",EDGE,"E13"),sQuery(id+"F0.wireOp",EDGE,"E14"),sQuery(id+"F0.wireOp",EDGE,"E15"),sQuery(id+"F0.wireOp",EDGE,"E17.filletArc"),sQuery(id+"F0.wireOp",EDGE,"E18.filletArc"),sQuery(id+"F0.wireOp",EDGE,"E19.filletArc"),sQuery(id+"F0.wireOp",EDGE,"E20.filletArc"),sQuery(id+"F0.wireOp",EDGE,"E25.0"),sQuery(id+"F0.wireOp",EDGE,"E25.1"),sQuery(id+"F0.wireOp",EDGE,"E25.2"),sQuery(id+"F0.wireOp",EDGE,"E25.3"),sQuery(id+"F0.wireOp",EDGE,"E25.4"),sQuery(id+"F0.wireOp",EDGE,"E25.5"),sQuery(id+"F0.wireOp",EDGE,"E25.6"),sQuery(id+"F0.wireOp",EDGE,"E25.7")])],"isStart":false});
            extrude(context, id + "F17", {"entities" : qUnion([Q0, Q1, Q2]), "endBound" : BoundingType.UP_TO_SURFACE, "depth" : 25 * mm, "endBoundEntityFace" : qUnion([Q3]), "offsetDistance" : 25 * mm});
        }
        {
            var Q0;
            {var subQ5=sQuery(id+"F16.wireOp",EDGE,"E96");Q0=makeQuery(id+"F16.imprint","IMPRINT",FACE,{"disambiguationData":[TD([[makeQuery(id+"F16.imprint","IMPRINT",EDGE,{"derivedFrom":subQ5}),1.0]])]});}
            var Q1;
            {var subQ1=sQuery(id+"F16.wireOp",EDGE,"E84");Q1=makeQuery(id+"F16.imprint","IMPRINT",FACE,{"disambiguationData":[TD([[makeQuery(id+"F16.imprint","IMPRINT",EDGE,{"derivedFrom":subQ1}),1.0]])]});}
            var Q2;
            Q2=makeQuery(id+"F16.imprint","IMPRINT",FACE,{"disambiguationData":[TD([[makeQuery(id+"F16.imprint","IMPRINT",EDGE,{"derivedFrom":sQuery(id+"F16.wireOp",EDGE,"E88.MirrorCS")}),1.0]])]});
            var Q3;
            {var subQ0=sQuery(id+"F4.wireOp",EDGE,"E36.filletArc");var subQ1=sQuery(id+"F4.wireOp",EDGE,"E35.filletArc");var subQ2=sQuery(id+"F4.wireOp",EDGE,"E34.filletArc");var subQ3=sQuery(id+"F4.wireOp",EDGE,"E33.filletArc");var subQ4=sQuery(id+"F4.wireOp",EDGE,"E27.0");var subQ5=sQuery(id+"F4.wireOp",EDGE,"E30");var subQ6=sQuery(id+"F4.wireOp",EDGE,"E28.0");var subQ7=sQuery(id+"F4.wireOp",EDGE,"E29");Q3=makeQuery(id+"F6.boolean.opBoolean","SPLIT",FACE,{"disambiguationData":[TD([makeQuery(id+"F5.opExtrude","SWEPT_FACE",FACE,{"disambiguationData":[OSD([subQ4])]})])],"derivedFrom":makeQuery(id+"F5.opExtrude","CAP_FACE",FACE,{"disambiguationData":[OSD([subQ4,subQ6,subQ7,subQ5,subQ3,subQ2,subQ1,subQ0,sQuery(id+"F4.wireOp",EDGE,"E41"),sQuery(id+"F4.wireOp",EDGE,"E42"),sQuery(id+"F4.wireOp",EDGE,"E43"),sQuery(id+"F4.wireOp",EDGE,"E45"),sQuery(id+"F4.wireOp",EDGE,"E46"),sQuery(id+"F4.wireOp",EDGE,"E47.filletArc"),sQuery(id+"F4.wireOp",EDGE,"E48.filletArc"),sQuery(id+"F4.wireOp",EDGE,"E49.filletArc"),sQuery(id+"F4.wireOp",EDGE,"E50.filletArc"),sQuery(id+"F4.wireOp",EDGE,"E51.filletArc"),sQuery(id+"F4.wireOp",EDGE,"E52.filletArc"),sQuery(id+"F4.wireOp",EDGE,"E53.0.MirrorCS"),sQuery(id+"F4.wireOp",EDGE,"E54.0.MirrorCS"),sQuery(id+"F4.wireOp",EDGE,"E55.0.MirrorCS"),sQuery(id+"F4.wireOp",EDGE,"E56.0.MirrorCS"),sQuery(id+"F4.wireOp",EDGE,"E57.0.MirrorCS"),sQuery(id+"F4.wireOp",EDGE,"E58.0.MirrorCS"),sQuery(id+"F4.wireOp",EDGE,"E59.0.MirrorCS"),sQuery(id+"F4.wireOp",EDGE,"E60.0.MirrorCS"),sQuery(id+"F4.wireOp",EDGE,"E61.0.MirrorCS"),sQuery(id+"F4.wireOp",EDGE,"E62.0.MirrorCS"),sQuery(id+"F4.wireOp",EDGE,"E63.0.MirrorCS")])],"isStart":true})});}
            extrude(context, id + "F18", {"entities" : qUnion([Q0, Q1, Q2]), "endBound" : BoundingType.UP_TO_SURFACE, "depth" : 25 * mm, "endBoundEntityFace" : qUnion([Q3]), "offsetDistance" : 25 * mm});
        }
        {
            var Q0;
            {var subQ0=sQuery(id+"F16.wireOp",EDGE,"E96");Q0=makeQuery(id+"F16.imprint","IMPRINT",FACE,{"disambiguationData":[TD([[makeQuery(id+"F16.imprint","IMPRINT",EDGE,{"derivedFrom":subQ0}),1.0]])]});}
            var Q1;
            Q1=makeQuery(id+"F16.imprint","IMPRINT",FACE,{"disambiguationData":[TD([[makeQuery(id+"F16.imprint","IMPRINT",EDGE,{"derivedFrom":sQuery(id+"F16.wireOp",EDGE,"E88.MirrorCS")}),1.0]])]});
            var Q2;
            {var subQ0=sQuery(id+"F16.wireOp",EDGE,"E84");Q2=makeQuery(id+"F16.imprint","IMPRINT",FACE,{"disambiguationData":[TD([[makeQuery(id+"F16.imprint","IMPRINT",EDGE,{"derivedFrom":subQ0}),1.0]])]});}
            var Q3;
            Q3=makeQuery(id+"F2.opExtrude","CAP_FACE",FACE,{"disambiguationData":[OSD([sQuery(id+"F0.wireOp",EDGE,"E12"),sQuery(id+"F0.wireOp",EDGE,"E13"),sQuery(id+"F0.wireOp",EDGE,"E14"),sQuery(id+"F0.wireOp",EDGE,"E15"),sQuery(id+"F0.wireOp",EDGE,"E17.filletArc"),sQuery(id+"F0.wireOp",EDGE,"E18.filletArc"),sQuery(id+"F0.wireOp",EDGE,"E19.filletArc"),sQuery(id+"F0.wireOp",EDGE,"E20.filletArc"),sQuery(id+"F0.wireOp",EDGE,"E25.0"),sQuery(id+"F0.wireOp",EDGE,"E25.1"),sQuery(id+"F0.wireOp",EDGE,"E25.2"),sQuery(id+"F0.wireOp",EDGE,"E25.3"),sQuery(id+"F0.wireOp",EDGE,"E25.4"),sQuery(id+"F0.wireOp",EDGE,"E25.5"),sQuery(id+"F0.wireOp",EDGE,"E25.6"),sQuery(id+"F0.wireOp",EDGE,"E25.7")])],"isStart":false});
            extrude(context, id + "F19", {"entities" : qUnion([Q0, Q1, Q2]), "endBound" : BoundingType.UP_TO_SURFACE, "depth" : 25 * mm, "endBoundEntityFace" : qUnion([Q3]), "offsetDistance" : 25 * mm});
        }
        {
            var Q0;
            Q0=makeQuery(id+"F19.opExtrude","SWEPT_BODY",BODY,{"disambiguationData":[OSD([sQuery(id+"F16.wireOp",EDGE,"E84"),sQuery(id+"F16.wireOp",EDGE,"E85"),sQuery(id+"F16.wireOp",EDGE,"E80"),sQuery(id+"F16.wireOp",EDGE,"E87.MirrorCS"),sQuery(id+"F16.wireOp",EDGE,"E82"),sQuery(id+"F16.wireOp",EDGE,"E83"),sQuery(id+"F16.wireOp",EDGE,"E88.MirrorCS"),sQuery(id+"F16.wireOp",EDGE,"E91.MirrorCS"),sQuery(id+"F16.wireOp",EDGE,"E92.MirrorCS"),sQuery(id+"F16.wireOp",EDGE,"E93.MirrorCS"),sQuery(id+"F16.wireOp",EDGE,"E89.MirrorC"),sQuery(id+"F16.wireOp",EDGE,"E90.MirrorCS"),sQuery(id+"F16.wireOp",EDGE,"E96"),sQuery(id+"F16.wireOp",EDGE,"E97"),sQuery(id+"F16.wireOp",EDGE,"E98"),sQuery(id+"F16.wireOp",EDGE,"E99"),sQuery(id+"F16.wireOp",EDGE,"E100"),sQuery(id+"F16.wireOp",EDGE,"E101"),sQuery(id+"F16.wireOp",EDGE,"E102"),sQuery(id+"F16.wireOp",EDGE,"E103"),sQuery(id+"F16.wireOp",EDGE,"E104"),sQuery(id+"F16.wireOp",EDGE,"E105"),sQuery(id+"F16.wireOp",EDGE,"E106"),sQuery(id+"F16.wireOp",EDGE,"E107"),sQuery(id+"F16.wireOp",EDGE,"E108"),sQuery(id+"F16.wireOp",EDGE,"E109"),sQuery(id+"F16.wireOp",EDGE,"E110"),sQuery(id+"F16.wireOp",EDGE,"E111"),sQuery(id+"F16.wireOp",EDGE,"E112"),sQuery(id+"F16.wireOp",EDGE,"E113"),sQuery(id+"F16.wireOp",EDGE,"E114"),sQuery(id+"F16.wireOp",EDGE,"E115"),sQuery(id+"F16.wireOp",EDGE,"E116"),sQuery(id+"F16.wireOp",EDGE,"E117"),sQuery(id+"F16.wireOp",EDGE,"E118")])]});
            deleteBodies(context, id + "F20", {"entities" : qUnion([Q0])});
        }
        {
            var Q0;
            {var subQ0=sQuery(id+"F16.wireOp",EDGE,"E96");Q0=makeQuery(id+"F16.imprint","IMPRINT",FACE,{"disambiguationData":[TD([[makeQuery(id+"F16.imprint","IMPRINT",EDGE,{"derivedFrom":subQ0}),1.0]])]});}
            var Q1;
            {var subQ0=sQuery(id+"F16.wireOp",EDGE,"E84");Q1=makeQuery(id+"F16.imprint","IMPRINT",FACE,{"disambiguationData":[TD([[makeQuery(id+"F16.imprint","IMPRINT",EDGE,{"derivedFrom":subQ0}),1.0]])]});}
            var Q2;
            Q2=makeQuery(id+"F16.imprint","IMPRINT",FACE,{"disambiguationData":[TD([[makeQuery(id+"F16.imprint","IMPRINT",EDGE,{"derivedFrom":sQuery(id+"F16.wireOp",EDGE,"E88.MirrorCS")}),1.0]])]});
            var Q3;
            Q3=makeQuery(id+"F2.opExtrude","CAP_FACE",FACE,{"disambiguationData":[OSD([sQuery(id+"F0.wireOp",EDGE,"E12"),sQuery(id+"F0.wireOp",EDGE,"E13"),sQuery(id+"F0.wireOp",EDGE,"E14"),sQuery(id+"F0.wireOp",EDGE,"E15"),sQuery(id+"F0.wireOp",EDGE,"E17.filletArc"),sQuery(id+"F0.wireOp",EDGE,"E18.filletArc"),sQuery(id+"F0.wireOp",EDGE,"E19.filletArc"),sQuery(id+"F0.wireOp",EDGE,"E20.filletArc"),sQuery(id+"F0.wireOp",EDGE,"E25.0"),sQuery(id+"F0.wireOp",EDGE,"E25.1"),sQuery(id+"F0.wireOp",EDGE,"E25.2"),sQuery(id+"F0.wireOp",EDGE,"E25.3"),sQuery(id+"F0.wireOp",EDGE,"E25.4"),sQuery(id+"F0.wireOp",EDGE,"E25.5"),sQuery(id+"F0.wireOp",EDGE,"E25.6"),sQuery(id+"F0.wireOp",EDGE,"E25.7")])],"isStart":false});
            extrude(context, id + "F21", {"entities" : qUnion([Q0, Q1, Q2]), "endBound" : BoundingType.UP_TO_SURFACE, "depth" : 25 * mm, "endBoundEntityFace" : qUnion([Q3]), "offsetDistance" : 25 * mm});
        }
    });
